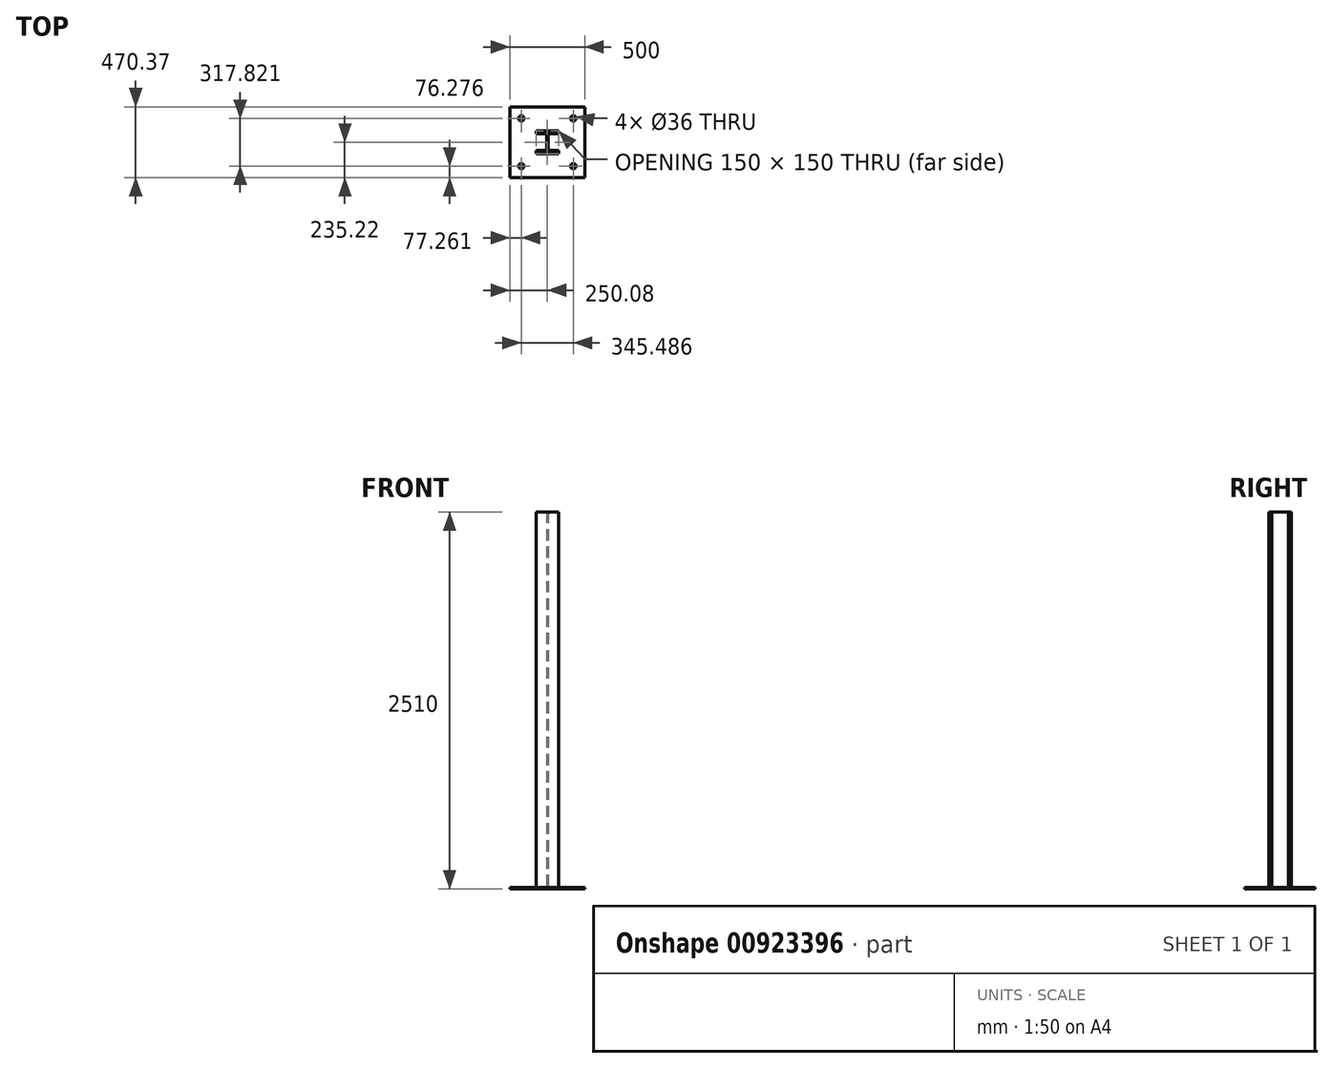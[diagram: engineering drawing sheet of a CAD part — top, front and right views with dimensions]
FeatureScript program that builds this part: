
annotation { "Feature Type Name" : "Feature", "Feature Type Description" : "" }
export const myFeature = defineFeature(function(context is Context, id is Id, definition is map)
    precondition{}
    {
        {
            var Q0;
            Q0=qCreatedBy(makeId("Top.planeOp"),FACE);
            var sketch = newSketch(context, id + "F0", { "sketchPlane" : qUnion([Q0])});
            skLineSegment(sketch, "E0.MirrorCS", {"start": v(116.39, -266.39) * mm, "end": v(116.39, -247.02) * mm});
            skLineSegment(sketch, "E1.MirrorCS", {"start": v(116.39, -116.39) * mm, "end": v(116.39, -135.76) * mm});
            skLineSegment(sketch, "E2.MirrorCS", {"start": v(191.39, -116.39) * mm, "end": v(116.39, -116.39) * mm});
            skLineSegment(sketch, "E3.MirrorCS", {"start": v(116.39, -135.76) * mm, "end": v(186.39, -135.76) * mm});
            skLineSegment(sketch, "E4.MirrorCS", {"start": v(116.39, -247.02) * mm, "end": v(186.39, -247.02) * mm});
            skPoint(sketch, "E5.MirrorCS.start.orphan", {"position": v(154.46, -191.39) * mm});
            skPoint(sketch, "E6.start.orphan", {"position": v(191.39, -191.39) * mm});
            skLineSegment(sketch, "E7", {"start": v(116.39, -266.39) * mm, "end": v(191.39, -266.39) * mm});
            skLineSegment(sketch, "E8.MirrorCS", {"start": v(186.39, -247.02) * mm, "end": v(186.39, -135.76) * mm});
            skPoint(sketch, "E9.orphan", {"position": v(196.39, -266.39) * mm});
            skPoint(sketch, "E10.orphan", {"position": v(186.39, -266.39) * mm});
            skLineSegment(sketch, "E11.MirrorCS", {"start": v(266.39, -116.39) * mm, "end": v(266.39, -135.76) * mm});
            skLineSegment(sketch, "E12.MirrorCS", {"start": v(266.39, -135.76) * mm, "end": v(196.39, -135.76) * mm});
            skLineSegment(sketch, "E13.MirrorCS", {"start": v(266.39, -266.39) * mm, "end": v(191.39, -266.39) * mm});
            skPoint(sketch, "E14.MirrorP", {"position": v(266.39, -244.95) * mm});
            skLineSegment(sketch, "E15.MirrorCS", {"start": v(266.39, -247.02) * mm, "end": v(196.39, -247.02) * mm});
            skLineSegment(sketch, "E16.MirrorCS", {"start": v(266.39, -266.39) * mm, "end": v(266.39, -247.02) * mm});
            skLineSegment(sketch, "E17.MirrorCS", {"start": v(191.39, -116.39) * mm, "end": v(266.39, -116.39) * mm});
            skLineSegment(sketch, "E18.MirrorCS", {"start": v(196.39, -247.02) * mm, "end": v(196.39, -135.76) * mm});
            skSolve(sketch);
        }
        {
            var Q0;
            Q0=makeQuery(id+"F0.imprint","IMPRINT",FACE,{"disambiguationData":[TD([[makeQuery(id+"F0.imprint","IMPRINT",EDGE,{"derivedFrom":sQuery(id+"F0.wireOp",EDGE,"E0.MirrorCS")}),-1.0]])]});
            extrude(context, id + "F1", {"entities" : qUnion([Q0]), "depth" : 2500 * mm, "offsetDistance" : 25.4 * mm});
        }
        {
            var Q0;
            Q0=makeQuery(id+"F0.imprint","IMPRINT",FACE,{"disambiguationData":[TD([[makeQuery(id+"F0.imprint","IMPRINT",EDGE,{"derivedFrom":sQuery(id+"F0.wireOp",EDGE,"E0.MirrorCS")}),-1.0]])]});
            var sketch = newSketch(context, id + "F2", { "sketchPlane" : qUnion([Q0])});
            skLineSegment(sketch, "E19.bottom", {"start": v(441.31, -426.6) * mm, "end": v(-58.69, -426.6) * mm});
            skLineSegment(sketch, "E19.top", {"start": v(441.31, 43.76) * mm, "end": v(-58.69, 43.76) * mm});
            skLineSegment(sketch, "E19.left", {"start": v(441.31, -426.6) * mm, "end": v(441.31, 43.76) * mm});
            skLineSegment(sketch, "E19.right", {"start": v(-58.69, -426.6) * mm, "end": v(-58.69, 43.76) * mm});
            skPoint(sketch, "E19.middle", {"position": v(191.31, -191.42) * mm});
            skSolve(sketch);
        }
        {
            var Q0;
            Q0=makeQuery(id+"F2.imprint","IMPRINT",FACE,{"disambiguationData":[TD([[makeQuery(id+"F2.imprint","IMPRINT",EDGE,{"derivedFrom":sQuery(id+"F2.wireOp",EDGE,"E19.bottom")}),-1.0]])]});
            extrude(context, id + "F3", {"entities" : qUnion([Q0]), "oppositeDirection" : true, "depth" : 10 * mm, "offsetDistance" : 25.4 * mm});
        }
        {
            var Q0;
            Q0=makeQuery(id+"F3.opExtrude","CAP_FACE",FACE,{"disambiguationData":[OSD([sQuery(id+"F0.wireOp",EDGE,"E0.MirrorCS"),sQuery(id+"F0.wireOp",EDGE,"E1.MirrorCS"),sQuery(id+"F0.wireOp",EDGE,"E2.MirrorCS"),sQuery(id+"F0.wireOp",EDGE,"E3.MirrorCS"),sQuery(id+"F0.wireOp",EDGE,"E4.MirrorCS"),sQuery(id+"F0.wireOp",EDGE,"E7"),sQuery(id+"F0.wireOp",EDGE,"E8.MirrorCS"),sQuery(id+"F0.wireOp",EDGE,"E11.MirrorCS"),sQuery(id+"F0.wireOp",EDGE,"E12.MirrorCS"),sQuery(id+"F0.wireOp",EDGE,"E13.MirrorCS"),sQuery(id+"F0.wireOp",EDGE,"E15.MirrorCS"),sQuery(id+"F0.wireOp",EDGE,"E16.MirrorCS"),sQuery(id+"F0.wireOp",EDGE,"E17.MirrorCS"),sQuery(id+"F0.wireOp",EDGE,"E18.MirrorCS"),sQuery(id+"F2.wireOp",EDGE,"E19.bottom"),sQuery(id+"F2.wireOp",EDGE,"E19.top"),sQuery(id+"F2.wireOp",EDGE,"E19.left"),sQuery(id+"F2.wireOp",EDGE,"E19.right")])],"isStart":true});
            var sketch = newSketch(context, id + "F4", { "sketchPlane" : qUnion([Q0])});
            skCircle(sketch, "E20", {"center": v(18.57, -32.51) * mm, "radius": 18.27 * mm});
            skLineSegment(sketch, "E21", {"start": v(191.31, 43.76) * mm, "end": v(191.31, -426.6) * mm});
            skLineSegment(sketch, "E22", {"start": v(-58.69, -191.42) * mm, "end": v(441.31, -191.42) * mm});
            skCircle(sketch, "E23.MirrorC", {"center": v(364.06, -32.51) * mm, "radius": 18.27 * mm});
            skCircle(sketch, "E24.MirrorC", {"center": v(18.57, -350.33) * mm, "radius": 18.27 * mm});
            skCircle(sketch, "E25.MirrorC", {"center": v(364.06, -350.33) * mm, "radius": 18.27 * mm});
            skSolve(sketch);
        }
        {
            var Q0;
            Q0=sQuery(id+"F4.wireOp",VERTEX,"E20.center");
            var Q1;
            Q1=sQuery(id+"F4.wireOp",VERTEX,"E24.MirrorC.center");
            var Q2;
            Q2=sQuery(id+"F4.wireOp",VERTEX,"E25.MirrorC.center");
            var Q3;
            Q3=sQuery(id+"F4.wireOp",VERTEX,"E23.MirrorC.center");
            var Q4;
            Q4=makeQuery(id+"F3.opExtrude","SWEPT_BODY",BODY,{"disambiguationData":[OSD([sQuery(id+"F0.wireOp",EDGE,"E0.MirrorCS"),sQuery(id+"F0.wireOp",EDGE,"E1.MirrorCS"),sQuery(id+"F0.wireOp",EDGE,"E2.MirrorCS"),sQuery(id+"F0.wireOp",EDGE,"E3.MirrorCS"),sQuery(id+"F0.wireOp",EDGE,"E4.MirrorCS"),sQuery(id+"F0.wireOp",EDGE,"E7"),sQuery(id+"F0.wireOp",EDGE,"E8.MirrorCS"),sQuery(id+"F0.wireOp",EDGE,"E11.MirrorCS"),sQuery(id+"F0.wireOp",EDGE,"E12.MirrorCS"),sQuery(id+"F0.wireOp",EDGE,"E13.MirrorCS"),sQuery(id+"F0.wireOp",EDGE,"E15.MirrorCS"),sQuery(id+"F0.wireOp",EDGE,"E16.MirrorCS"),sQuery(id+"F0.wireOp",EDGE,"E17.MirrorCS"),sQuery(id+"F0.wireOp",EDGE,"E18.MirrorCS"),sQuery(id+"F2.wireOp",EDGE,"E19.bottom"),sQuery(id+"F2.wireOp",EDGE,"E19.top"),sQuery(id+"F2.wireOp",EDGE,"E19.left"),sQuery(id+"F2.wireOp",EDGE,"E19.right")])]});
            hole(context, id + "F5", {"style" : HoleStyle.SIMPLE, "endStyle" : HoleEndStyle.THROUGH, "holeDiameter" : 36 * mm, "majorDiameter" : 6.35 * mm, "isTappedThrough" : true, "tappedDepth" : 12.7 * mm, "tapClearance" : 3, "locations" : qUnion([Q0, Q1, Q2, Q3]), "scope" : qUnion([Q4])});
        }
    });
